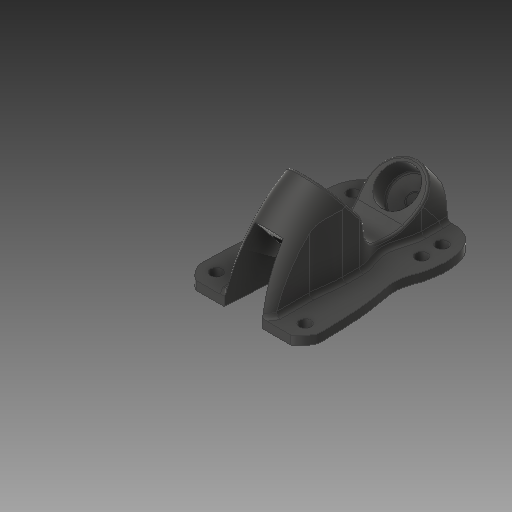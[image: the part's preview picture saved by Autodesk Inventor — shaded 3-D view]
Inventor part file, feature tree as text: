
AUTODESK INVENTOR PART (.ipt)
format: ipt  version: 2019.3 (Build 233278000, 278)  size: 4,589,056 bytes
history: native  units: mm
features: sketch x10, extrude x7, fillet x6, other x5, plane x2, revolve x1, emboss x1, loft x1
ambient origin geometry x8: Origin, YZ Plane, XZ Plane, XY Plane, X Axis, Y Axis, Z Axis, Center Point
bodies: Solid1 (feature_tree)
feature tree (33):
  extrude  "Extrusion8"  Depth=87.0mm
  extrude  "Extrusion11"  Depth=49.0mm
  sketch  "Sketch21"  dims[d14=41.3mm d15=49.0mm d16=57.0mm]
  fillet  "Fillet10"  Radius=57.0mm
  extrude  "Extrusion12"  Depth=80.0mm
  extrude  "Extrusion13"  Depth=20.0mm
  fillet  "Fillet11"  Radius=40.0mm
  extrude  "Extrusion14"  Depth=3.0mm
  extrude  "Extrusion15"  Depth=64.0mm
  plane  "Work Plane14"
  revolve  "Revolution2"  [1 undecoded]
  extrude  "Extrusion16"  Depth=12.5mm
  fillet  "Fillet12"  Radius=25.0mm
  fillet  "Fillet13"  Radius=25.0mm
  emboss  "Emboss2"
  plane  "Work Plane15"
  other  "Work Axis4"
  other  "Work Point1"
  loft  "Loft3"
  fillet  "Fillet16"  Radius=25.0mm
  fillet  "Fillet17"  Radius=11.0mm
  other  "Image6"
  sketch  "Sketch20"  dims[d5=5.5mm d6=5.5mm d7=5.5mm d10=54.0mm d11=63.5mm d13=87.0mm]
  other  "Image10"
  sketch  "Sketch22"  dims[d17=55.0mm d345=80.0mm]
  sketch  "Sketch23"  dims[d380=4.0mm d381=0.0mm d568=20.0mm d571=40.0mm]
  sketch  "Sketch25"  dims[d583=7.0mm d589=3.0mm]
  sketch  "Sketch26"  dims[d608=3.5mm d609=64.0mm]
  other  "Work Axis3"
  sketch  "Sketch27"  dims[d612=6.747409mm d634=12.0mm]
  sketch  "Sketch29"  dims[d646=25.0mm d647=0.0mm d651=12.5mm d652=25.0mm d653=0.0mm d654=25.0mm d655=0.0mm]
  sketch  "Sketch30"  dims[d656=12.5mm d666=9.0mm d668=25.0mm d669=0.0mm d670=11.0mm]
  sketch  "Sketch31"  dims[d671=18.0mm d672=12.0mm d673=0.0mm d674=90.0deg d675=90.0deg d676=19.0mm d677=0.0mm d678=0.0mm d679=1.0mm d680=2.0mm d682=1.0mm d683=0.0mm d684=-21.5mm d685=6.5mm d693=1.0mm d694=0.0mm d695=90.0deg d696=0.0mm d697=90.0deg d698=2.0mm d699=0.5mm d700=9.5mm d703=23.0mm]
note: 1 required parameter value undecoded (feature->parameter linkage not recoverable at this tier; creation-order binding heuristic only, values carry confidence <= 0.55)
